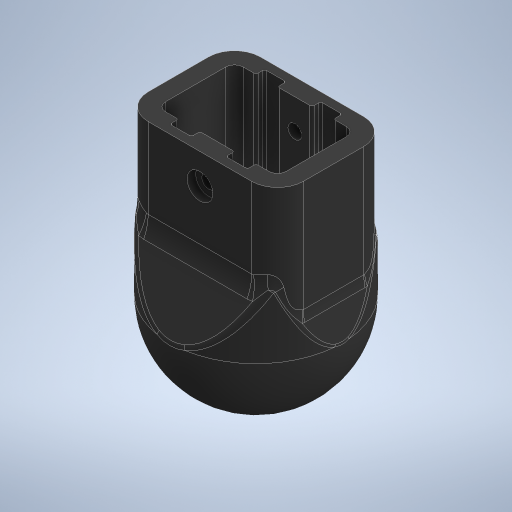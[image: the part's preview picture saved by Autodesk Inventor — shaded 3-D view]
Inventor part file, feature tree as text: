
AUTODESK INVENTOR PART (.ipt)
format: ipt  version: 2024.3 (Build 283343000, 343)  size: 886,784 bytes
history: native  units: mm
features: sketch x19, extrude x18, projected_geometry x7, fillet x6, other x1, revolve x1
ambient origin geometry x8: Origin, YZ Plane, XZ Plane, XY Plane, X Axis, Y Axis, Z Axis, Center Point
bodies: Body1 (feature_tree)
feature tree (52):
  other  "ソリッド1"
  extrude  "押し出し1"  Depth=40.0mm
  extrude  "押し出し2"  Depth=10.0mm
  extrude  "押し出し3"  Depth=10.0mm
  fillet  "フィレット1"  Radius=50.0mm
  extrude  "押し出し7"  Depth=10.0mm
  revolve  "回転2"
  extrude  "押し出し8"  Depth=30.0mm
  extrude  "押し出し9"  Depth=5.2mm
  extrude  "押し出し10"  Depth=5.2mm
  extrude  "押し出し11"  Depth=20.0mm
  extrude  "押し出し12"  Depth=22.0mm TaperAngle=0.0deg
  extrude  "押し出し13"  Depth=120.0mm
  extrude  "押し出し14"  Depth=20.0mm
  extrude  "押し出し15"  Depth=50.0mm
  extrude  "押し出し16"  Depth=25.0mm
  fillet  "フィレット3"  Radius=10.0mm
  fillet  "フィレット4"  Radius=10.0mm
  fillet  "フィレット5"  Radius=5.0mm
  extrude  "押し出し18"  Depth=20.0mm
  fillet  "フィレット7"  Radius=50.0mm
  extrude  "押し出し19"  Depth=5.0mm TaperAngle=0.0deg
  extrude  "押し出し20"  Depth=35.0mm
  fillet  "フィレット8"  Radius=2.0mm
  extrude  "押し出し21"  Depth=10.0mm
  extrude  "押し出し22"  Depth=30.0mm
  sketch  "スケッチ1"
  sketch  "スケッチ2"
  sketch  "スケッチ3"
  sketch  "スケッチ8"
  sketch  "スケッチ9"
  sketch  "スケッチ10"
  projected_geometry  "投影ループ2"
  sketch  "スケッチ11"
  sketch  "スケッチ12"
  sketch  "スケッチ13"
  sketch  "スケッチ15"
  sketch  "スケッチ16"
  sketch  "スケッチ17"
  sketch  "スケッチ19"
  projected_geometry  "投影ループ3"
  projected_geometry  "投影ループ4"
  projected_geometry  "投影ループ5"
  projected_geometry  "投影ループ6"
  projected_geometry  "投影ループ7"
  sketch  "スケッチ20"
  sketch  "スケッチ22"
  projected_geometry  "投影ループ8"
  sketch  "スケッチ23"
  sketch  "スケッチ25"
  sketch  "スケッチ26"
  sketch  "スケッチ27"
